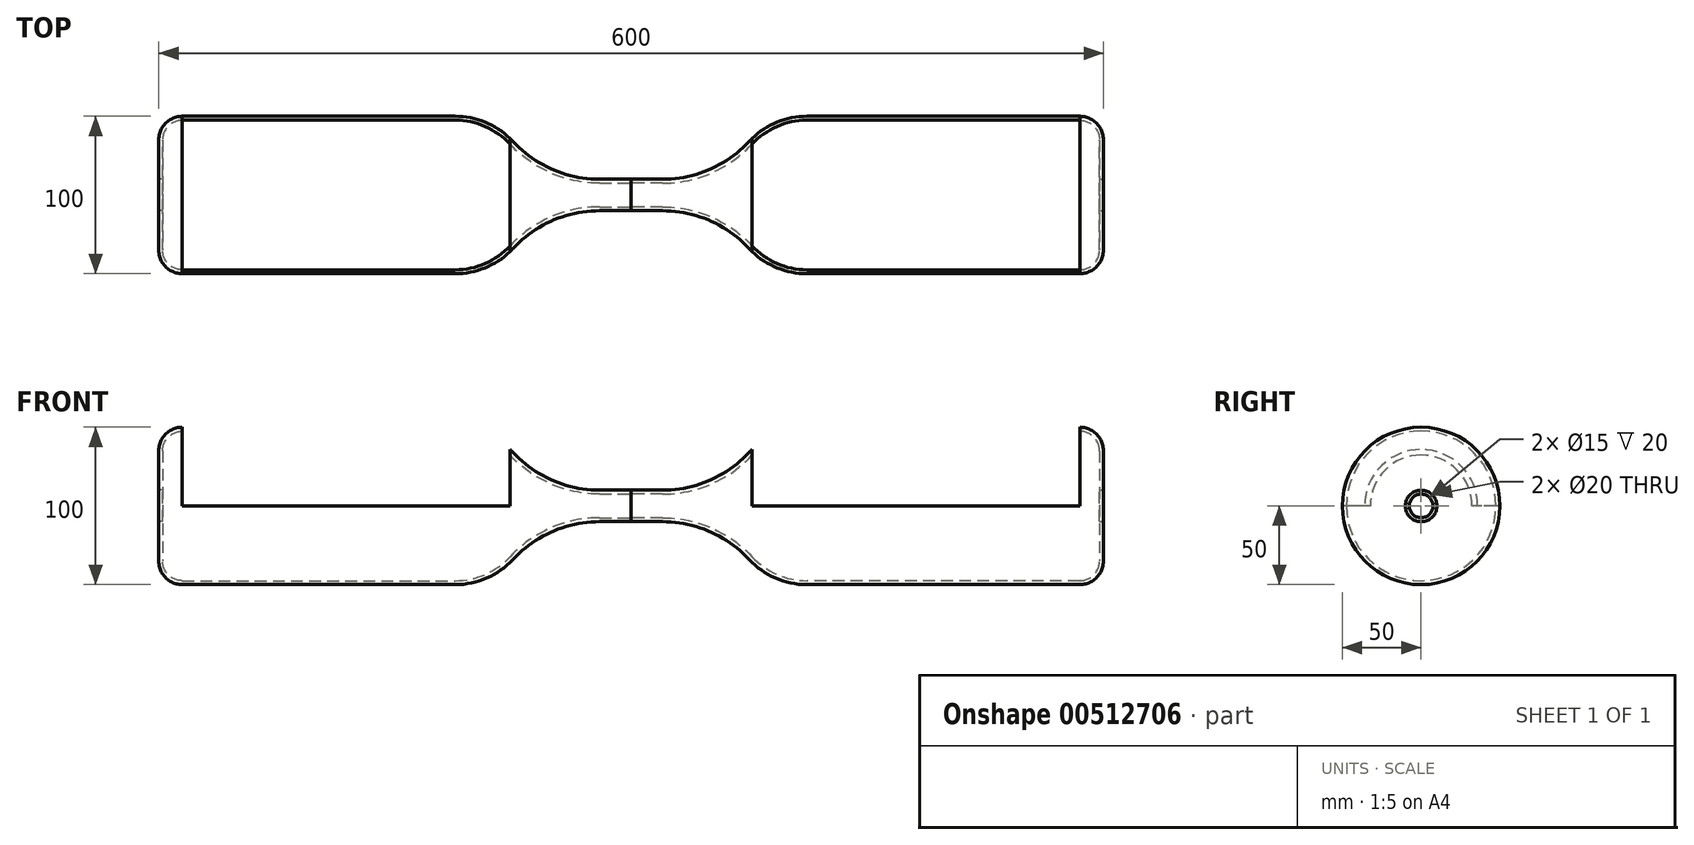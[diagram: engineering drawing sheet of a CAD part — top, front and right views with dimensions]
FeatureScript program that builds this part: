
annotation { "Feature Type Name" : "Feature", "Feature Type Description" : "" }
export const myFeature = defineFeature(function(context is Context, id is Id, definition is map)
    precondition{}
    {
        {
            var Q0;
            Q0=qCreatedBy(makeId("Front.planeOp"),FACE);
            var sketch = newSketch(context, id + "F0", { "sketchPlane" : qUnion([Q0])});
            skLineSegment(sketch, "E0", {"start": v(-111.65, 0) * mm, "end": v(-111.65, -10) * mm});
            skLineSegment(sketch, "E1", {"start": v(-111.65, -10) * mm, "end": v(-91.65, -10) * mm});
            skArc(sketch, "E2", {"start": v(-36.66, -34) * mm, "mid": v(-61.65, -16.26) * mm, "end": v(-91.65, -10) * mm});
            skArc(sketch, "E3", {"start": v(-36.66, -34) * mm, "mid": v(-20, -45.83) * mm, "end": v(0, -50) * mm});
            skLineSegment(sketch, "E4", {"start": v(0, -50) * mm, "end": v(173.35, -50) * mm});
            skArc(sketch, "E5", {"start": v(173.35, -50) * mm, "mid": v(183.96, -45.6) * mm, "end": v(188.35, -35) * mm});
            skLineSegment(sketch, "E6", {"start": v(188.35, -35) * mm, "end": v(188.35, 0) * mm});
            skLineSegment(sketch, "E7", {"start": v(-111.65, 0) * mm, "end": v(188.35, 0) * mm});
            skSolve(sketch);
        }
        {
            var Q0;
            Q0=makeQuery(id+"F0.imprint","IMPRINT",FACE,{"disambiguationData":[TD([[makeQuery(id+"F0.imprint","IMPRINT",EDGE,{"derivedFrom":sQuery(id+"F0.wireOp",EDGE,"E0")}),1.0]])]});
            var Q1;
            Q1=sQuery(id+"F0.wireOp",EDGE,"E7");
            revolve(context, id + "F1", {"entities" : qUnion([Q0]), "axis" : qUnion([Q1]), "revolveType" : RevolveType.FULL});
        }
        {
            var Q0;
            Q0=makeQuery(id+"F1.opRevolve","SWEPT_FACE",FACE,{"disambiguationData":[OSD([sQuery(id+"F0.wireOp",EDGE,"E0")])]});
            shell(context, id + "F2", {"entities" : qUnion([Q0]), "thickness" : 2.5 * mm});
        }
        {
            var Q0;
            Q0=qCreatedBy(makeId("Top.planeOp"),FACE);
            var sketch = newSketch(context, id + "F3", { "sketchPlane" : qUnion([Q0])});
            skLineSegment(sketch, "E8.bottom", {"start": v(-34.83, 75.84) * mm, "end": v(173.35, 75.84) * mm});
            skLineSegment(sketch, "E8.top", {"start": v(-34.83, -65.43) * mm, "end": v(173.35, -65.43) * mm});
            skLineSegment(sketch, "E8.left", {"start": v(-34.83, 75.84) * mm, "end": v(-34.83, -65.43) * mm});
            skLineSegment(sketch, "E8.right", {"start": v(173.35, 75.84) * mm, "end": v(173.35, -65.43) * mm});
            skSolve(sketch);
        }
        {
            var Q0;
            Q0 = qSketchRegion(id + "F3", true);
            extrude(context, id + "F4", {"entities" : qUnion([Q0]), "operationType" : NewBodyOperationType.REMOVE, "depth" : 113 * mm});
        }
        {
            var Q0;
            Q0=makeQuery(id+"F1.opRevolve","SWEPT_FACE",FACE,{"disambiguationData":[OSD([sQuery(id+"F0.wireOp",EDGE,"E6")])]});
            var sketch = newSketch(context, id + "F5", { "sketchPlane" : qUnion([Q0])});
            skCircle(sketch, "E9", {"center": v(0, 0) * mm, "radius": 10 * mm});
            skSolve(sketch);
        }
        {
            var Q0;
            Q0 = qSketchRegion(id + "F5", true);
            extrude(context, id + "F6", {"entities" : qUnion([Q0]), "operationType" : NewBodyOperationType.REMOVE, "oppositeDirection" : true, "depth" : 25 * mm});
        }
        {
            var Q0;
            Q0=makeQuery(id+"F1.opRevolve","SWEPT_BODY",BODY,{"disambiguationData":[OSD([sQuery(id+"F0.wireOp",EDGE,"E0"),sQuery(id+"F0.wireOp",EDGE,"E1"),sQuery(id+"F0.wireOp",EDGE,"E2"),sQuery(id+"F0.wireOp",EDGE,"E3"),sQuery(id+"F0.wireOp",EDGE,"E4"),sQuery(id+"F0.wireOp",EDGE,"E5"),sQuery(id+"F0.wireOp",EDGE,"E6"),sQuery(id+"F0.wireOp",EDGE,"E7")])]});
            var Q1;
            Q1=makeQuery(id+"F1.opRevolve","SWEPT_FACE",FACE,{"disambiguationData":[OSD([sQuery(id+"F0.wireOp",EDGE,"E0")])]});
            mirror(context, id + "F7", {"entities" : qUnion([Q0]), "mirrorPlane" : qUnion([Q1])});
        }
    });
